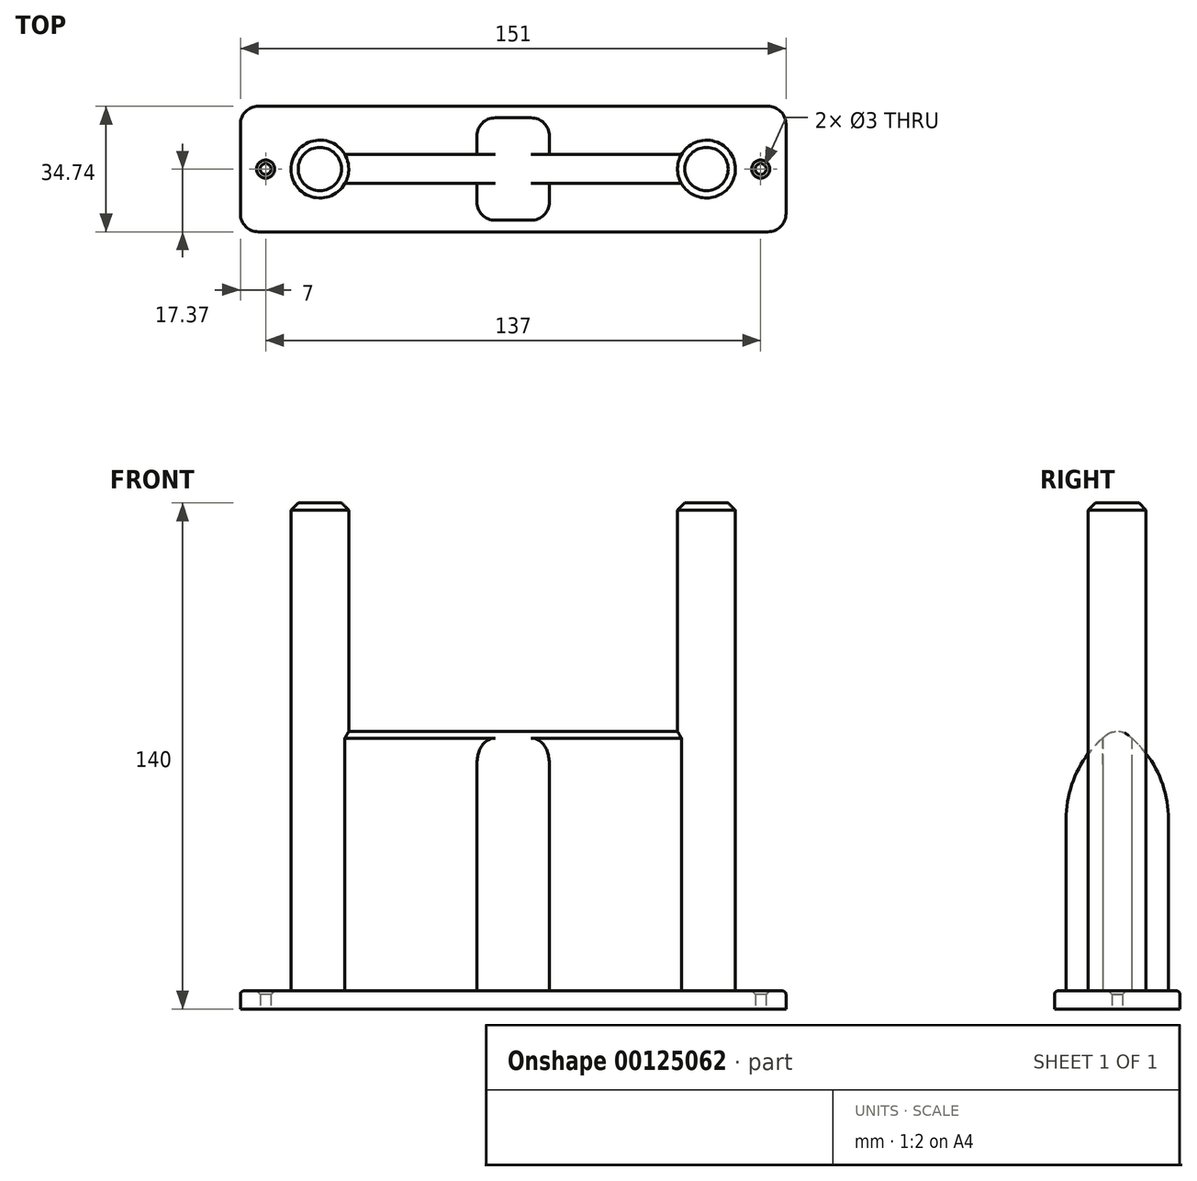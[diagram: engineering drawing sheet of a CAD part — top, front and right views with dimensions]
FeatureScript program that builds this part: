
annotation { "Feature Type Name" : "Feature", "Feature Type Description" : "" }
export const myFeature = defineFeature(function(context is Context, id is Id, definition is map)
    precondition{}
    {
        {
            var Q0;
            Q0=qCreatedBy(makeId("Top.planeOp"),FACE);
            var sketch = newSketch(context, id + "F0", { "sketchPlane" : qUnion([Q0])});
            skCircle(sketch, "E0", {"center": v(-53.5, 0) * mm, "radius": 8 * mm});
            skCircle(sketch, "E1", {"center": v(53.5, 0) * mm, "radius": 8 * mm});
            skLineSegment(sketch, "E2.bottom", {"start": v(-70.5, 17.37) * mm, "end": v(70.5, 17.37) * mm});
            skLineSegment(sketch, "E2.top", {"start": v(-70.5, -17.37) * mm, "end": v(70.5, -17.37) * mm});
            skLineSegment(sketch, "E2.left", {"start": v(-75.5, 12.37) * mm, "end": v(-75.5, -12.37) * mm});
            skLineSegment(sketch, "E2.right", {"start": v(75.5, 12.37) * mm, "end": v(75.5, -12.37) * mm});
            skPoint(sketch, "E2.middle", {"position": v(0, 0) * mm});
            skPoint(sketch, "E3.visualSharp", {"position": v(-75.5, 17.37) * mm});
            skArc(sketch, "E3.filletArc", {"start": v(-70.5, 17.37) * mm, "mid": v(-74.04, 15.9) * mm, "end": v(-75.5, 12.37) * mm});
            skPoint(sketch, "E4.visualSharp", {"position": v(75.5, 17.37) * mm});
            skArc(sketch, "E4.filletArc", {"start": v(75.5, 12.37) * mm, "mid": v(74.04, 15.9) * mm, "end": v(70.5, 17.37) * mm});
            skPoint(sketch, "E5.visualSharp", {"position": v(75.5, -17.37) * mm});
            skArc(sketch, "E5.filletArc", {"start": v(70.5, -17.37) * mm, "mid": v(74.04, -15.9) * mm, "end": v(75.5, -12.37) * mm});
            skPoint(sketch, "E6.visualSharp", {"position": v(-75.5, -17.37) * mm});
            skArc(sketch, "E6.filletArc", {"start": v(-75.5, -12.37) * mm, "mid": v(-74.04, -15.9) * mm, "end": v(-70.5, -17.37) * mm});
            skCircle(sketch, "E7", {"center": v(-68.5, 0) * mm, "radius": 1.5 * mm});
            skCircle(sketch, "E8", {"center": v(68.5, 0) * mm, "radius": 1.5 * mm});
            skLineSegment(sketch, "E9.bottom", {"start": v(-53.5, 4) * mm, "end": v(53.5, 4) * mm});
            skLineSegment(sketch, "E9.top", {"start": v(-53.5, -4) * mm, "end": v(53.5, -4) * mm});
            skLineSegment(sketch, "E9.left", {"start": v(-53.5, 4) * mm, "end": v(-53.5, -4) * mm});
            skLineSegment(sketch, "E9.right", {"start": v(53.5, 4) * mm, "end": v(53.5, -4) * mm});
            skLineSegment(sketch, "E10.bottom", {"start": v(10.01, 14.16) * mm, "end": v(-10.01, 14.16) * mm});
            skLineSegment(sketch, "E10.top", {"start": v(10.01, -14.16) * mm, "end": v(-10.01, -14.16) * mm});
            skLineSegment(sketch, "E10.left", {"start": v(10.01, 14.16) * mm, "end": v(10.01, -14.16) * mm});
            skLineSegment(sketch, "E10.right", {"start": v(-10.01, 14.16) * mm, "end": v(-10.01, -14.16) * mm});
            skSolve(sketch);
        }
        {
            var Q0;
            Q0=makeQuery(id+"F0.imprint","IMPRINT",FACE,{"disambiguationData":[TD([[makeQuery(id+"F0.imprint","IMPRINT",EDGE,{"derivedFrom":sQuery(id+"F0.wireOp",EDGE,"E0")}),-1.0]])]});
            var Q1;
            Q1=makeQuery(id+"F0.imprint","IMPRINT",FACE,{"disambiguationData":[TD([[makeQuery(id+"F0.imprint","IMPRINT",EDGE,{"derivedFrom":sQuery(id+"F0.wireOp",EDGE,"E2.bottom")}),-1.0]])]});
            var Q2;
            {var subQ5=sQuery(id+"F0.wireOp",EDGE,"E10.bottom");Q2=makeQuery(id+"F0.imprint","IMPRINT",FACE,{"disambiguationData":[TD([[makeQuery(id+"F0.imprint","IMPRINT",EDGE,{"derivedFrom":subQ5}),1.0]])]});}
            var Q3;
            {var subQ0=sQuery(id+"F0.wireOp",EDGE,"E10.right");var subQ1=sQuery(id+"F0.wireOp",EDGE,"E9.bottom");var subQ2=makeQuery(id+"F0.imprint","INTERSECT",VERTEX,{"derivedFrom":[subQ1,subQ0]});Q3=makeQuery(id+"F0.imprint","IMPRINT",FACE,{"disambiguationData":[TD([[makeQuery(id+"F0.imprint","IMPRINT",EDGE,{"disambiguationData":[TD([[subQ2,-1.0]])],"derivedFrom":subQ1}),-1.0]])]});}
            var Q4;
            {var subQ0=sQuery(id+"F0.wireOp",EDGE,"E9.bottom");var subQ1=sQuery(id+"F0.wireOp",EDGE,"E1");var subQ2=makeQuery(id+"F0.imprint","INTERSECT",VERTEX,{"derivedFrom":[subQ1,subQ0]});Q4=makeQuery(id+"F0.imprint","IMPRINT",FACE,{"disambiguationData":[TD([[makeQuery(id+"F0.imprint","IMPRINT",EDGE,{"disambiguationData":[TD([[subQ2,-1.0]])],"derivedFrom":subQ1}),-1.0]])]});}
            var Q5;
            {var subQ5=sQuery(id+"F0.wireOp",EDGE,"E10.top");Q5=makeQuery(id+"F0.imprint","IMPRINT",FACE,{"disambiguationData":[TD([[makeQuery(id+"F0.imprint","IMPRINT",EDGE,{"derivedFrom":subQ5}),-1.0]])]});}
            extrude(context, id + "F1", {"entities" : qUnion([Q0, Q1, Q2, Q3, Q4, Q5]), "depth" : 5 * mm});
        }
        {
            var Q0;
            Q0=makeQuery(id+"F0.imprint","IMPRINT",FACE,{"disambiguationData":[TD([[makeQuery(id+"F0.imprint","IMPRINT",EDGE,{"derivedFrom":sQuery(id+"F0.wireOp",EDGE,"E0")}),1.0]])]});
            var Q1;
            Q1=makeQuery(id+"F0.imprint","IMPRINT",FACE,{"disambiguationData":[TD([[makeQuery(id+"F0.imprint","IMPRINT",EDGE,{"derivedFrom":sQuery(id+"F0.wireOp",EDGE,"E1")}),1.0]])]});
            extrude(context, id + "F2", {"entities" : qUnion([Q0, Q1]), "operationType" : NewBodyOperationType.ADD, "depth" : 140 * mm});
        }
        {
            var Q0;
            Q0=makeQuery(id+"F2.opExtrude","CAP_EDGE",EDGE,{"disambiguationData":[OSD([sQuery(id+"F0.wireOp",EDGE,"E0")])],"isStart":false});
            var Q1;
            Q1=makeQuery(id+"F2.opExtrude","CAP_EDGE",EDGE,{"disambiguationData":[OSD([sQuery(id+"F0.wireOp",EDGE,"E1")])],"isStart":false});
            chamfer(context, id + "F3", {"entities" : qUnion([Q0, Q1]), "width" : 2 * mm, "tangentPropagation" : true});
        }
        {
            var Q0;
            Q0=makeQuery(id+"F1.opExtrude","CAP_EDGE",EDGE,{"disambiguationData":[OSD([sQuery(id+"F0.wireOp",EDGE,"E7")])],"isStart":false});
            var Q1;
            Q1=makeQuery(id+"F1.opExtrude","CAP_EDGE",EDGE,{"disambiguationData":[OSD([sQuery(id+"F0.wireOp",EDGE,"E8")])],"isStart":false});
            chamfer(context, id + "F4", {"entities" : qUnion([Q0, Q1]), "width" : 1 * mm, "tangentPropagation" : true});
        }
        {
            var Q0;
            Q0=makeQuery(id+"F1.opExtrude","CAP_EDGE",EDGE,{"disambiguationData":[OSD([sQuery(id+"F0.wireOp",EDGE,"E2.top")])],"isStart":false});
            fillet(context, id + "F5", {"entities" : qUnion([Q0]), "radius" : 1 * mm, "tangentPropagation" : true, "allowEdgeOverflow" : false});
        }
        {
            var Q0;
            {var subQ0=sQuery(id+"F0.wireOp",EDGE,"E9.bottom");var subQ1=sQuery(id+"F0.wireOp",EDGE,"E0");var subQ2=makeQuery(id+"F0.imprint","INTERSECT",VERTEX,{"derivedFrom":[subQ1,subQ0]});Q0=makeQuery(id+"F0.imprint","IMPRINT",FACE,{"disambiguationData":[TD([[makeQuery(id+"F0.imprint","IMPRINT",EDGE,{"disambiguationData":[TD([[subQ2,1.0]])],"derivedFrom":subQ1}),-1.0]])]});}
            var Q1;
            {var subQ0=sQuery(id+"F0.wireOp",EDGE,"E10.right");var subQ1=sQuery(id+"F0.wireOp",EDGE,"E9.bottom");var subQ2=makeQuery(id+"F0.imprint","INTERSECT",VERTEX,{"derivedFrom":[subQ1,subQ0]});Q1=makeQuery(id+"F0.imprint","IMPRINT",FACE,{"disambiguationData":[TD([[makeQuery(id+"F0.imprint","IMPRINT",EDGE,{"disambiguationData":[TD([[subQ2,-1.0]])],"derivedFrom":subQ1}),-1.0]])]});}
            var Q2;
            {var subQ0=sQuery(id+"F0.wireOp",EDGE,"E9.bottom");var subQ1=sQuery(id+"F0.wireOp",EDGE,"E1");var subQ2=makeQuery(id+"F0.imprint","INTERSECT",VERTEX,{"derivedFrom":[subQ1,subQ0]});Q2=makeQuery(id+"F0.imprint","IMPRINT",FACE,{"disambiguationData":[TD([[makeQuery(id+"F0.imprint","IMPRINT",EDGE,{"disambiguationData":[TD([[subQ2,-1.0]])],"derivedFrom":subQ1}),-1.0]])]});}
            var Q3;
            {var subQ5=sQuery(id+"F0.wireOp",EDGE,"E10.bottom");Q3=makeQuery(id+"F0.imprint","IMPRINT",FACE,{"disambiguationData":[TD([[makeQuery(id+"F0.imprint","IMPRINT",EDGE,{"derivedFrom":subQ5}),1.0]])]});}
            var Q4;
            {var subQ5=sQuery(id+"F0.wireOp",EDGE,"E10.top");Q4=makeQuery(id+"F0.imprint","IMPRINT",FACE,{"disambiguationData":[TD([[makeQuery(id+"F0.imprint","IMPRINT",EDGE,{"derivedFrom":subQ5}),-1.0]])]});}
            extrude(context, id + "F6", {"entities" : qUnion([Q0, Q1, Q2, Q3, Q4]), "operationType" : NewBodyOperationType.ADD, "depth" : 80 * mm});
        }
        {
            var Q0;
            Q0=makeQuery(id+"F6.opExtrude","CAP_EDGE",EDGE,{"disambiguationData":[OSD([sQuery(id+"F0.wireOp",EDGE,"E10.top")])],"isStart":false});
            var Q1;
            Q1=makeQuery(id+"F6.opExtrude","CAP_EDGE",EDGE,{"disambiguationData":[OSD([sQuery(id+"F0.wireOp",EDGE,"E10.bottom")])],"isStart":false});
            fillet(context, id + "F7", {"entities" : qUnion([Q0, Q1]), "radius" : 30 * mm, "allowEdgeOverflow" : false});
        }
        {
            var Q0;
            Q0=makeQuery(id+"F7.opFillet","BLEND_EDGE",EDGE,{"blendedFrom":[makeQuery(id+"F6.opExtrude","CAP_EDGE",EDGE,{"disambiguationData":[OSD([sQuery(id+"F0.wireOp",EDGE,"E10.bottom")])],"isStart":false}),makeQuery(id+"F6.opExtrude","CAP_EDGE",EDGE,{"disambiguationData":[OSD([sQuery(id+"F0.wireOp",EDGE,"E10.top")])],"isStart":false})],"blendedInto":[]});
            fillet(context, id + "F8", {"entities" : qUnion([Q0]), "radius" : 5 * mm, "tangentPropagation" : true, "allowEdgeOverflow" : false});
        }
        {
            var Q0;
            {var subQ0=sQuery(id+"F0.wireOp",EDGE,"E10.left");var subQ1=sQuery(id+"F0.wireOp",EDGE,"E10.bottom");Q0=makeQuery(id+"F7.opFillet","BLEND_EDGE",EDGE,{"blendedFrom":[makeQuery(id+"F6.opExtrude","CAP_EDGE",EDGE,{"disambiguationData":[OSD([subQ1])],"isStart":false}),makeQuery(id+"F6.opExtrude","SWEPT_FACE",FACE,{"disambiguationData":[OSD([subQ0]),TDD([makeQuery(id+"F0.imprint","IMPRINT",EDGE,{"disambiguationData":[TD([[makeQuery(id+"F0.imprint","INTERSECT",VERTEX,{"derivedFrom":[subQ1,subQ0]}),-1.0]])],"derivedFrom":subQ0})])]})],"blendedInto":[makeQuery(id+"F6.opExtrude","SWEPT_FACE",FACE,{"disambiguationData":[OSD([subQ0]),TDD([makeQuery(id+"F0.imprint","IMPRINT",EDGE,{"disambiguationData":[TD([[makeQuery(id+"F0.imprint","INTERSECT",VERTEX,{"derivedFrom":[subQ1,subQ0]}),-1.0]])],"derivedFrom":subQ0})])]})]});}
            var Q1;
            {var subQ0=sQuery(id+"F0.wireOp",EDGE,"E10.right");var subQ1=sQuery(id+"F0.wireOp",EDGE,"E10.bottom");Q1=makeQuery(id+"F7.opFillet","BLEND_EDGE",EDGE,{"blendedFrom":[makeQuery(id+"F6.opExtrude","CAP_EDGE",EDGE,{"disambiguationData":[OSD([subQ1])],"isStart":false}),makeQuery(id+"F6.opExtrude","SWEPT_FACE",FACE,{"disambiguationData":[OSD([subQ0]),TDD([makeQuery(id+"F0.imprint","IMPRINT",EDGE,{"disambiguationData":[TD([[makeQuery(id+"F0.imprint","INTERSECT",VERTEX,{"derivedFrom":[subQ1,subQ0]}),-1.0]])],"derivedFrom":subQ0})])]})],"blendedInto":[makeQuery(id+"F6.opExtrude","SWEPT_FACE",FACE,{"disambiguationData":[OSD([subQ0]),TDD([makeQuery(id+"F0.imprint","IMPRINT",EDGE,{"disambiguationData":[TD([[makeQuery(id+"F0.imprint","INTERSECT",VERTEX,{"derivedFrom":[subQ1,subQ0]}),-1.0]])],"derivedFrom":subQ0})])]})]});}
            var Q2;
            {var subQ0=sQuery(id+"F0.wireOp",EDGE,"E10.left");var subQ1=sQuery(id+"F0.wireOp",EDGE,"E10.top");Q2=makeQuery(id+"F7.opFillet","BLEND_EDGE",EDGE,{"blendedFrom":[makeQuery(id+"F6.opExtrude","CAP_EDGE",EDGE,{"disambiguationData":[OSD([subQ1])],"isStart":false}),makeQuery(id+"F6.opExtrude","SWEPT_FACE",FACE,{"disambiguationData":[OSD([subQ0]),TDD([makeQuery(id+"F0.imprint","IMPRINT",EDGE,{"disambiguationData":[TD([[makeQuery(id+"F0.imprint","INTERSECT",VERTEX,{"derivedFrom":[subQ1,subQ0]}),1.0]])],"derivedFrom":subQ0})])]})],"blendedInto":[makeQuery(id+"F6.opExtrude","SWEPT_FACE",FACE,{"disambiguationData":[OSD([subQ0]),TDD([makeQuery(id+"F0.imprint","IMPRINT",EDGE,{"disambiguationData":[TD([[makeQuery(id+"F0.imprint","INTERSECT",VERTEX,{"derivedFrom":[subQ1,subQ0]}),1.0]])],"derivedFrom":subQ0})])]})]});}
            var Q3;
            {var subQ0=sQuery(id+"F0.wireOp",EDGE,"E10.right");var subQ1=sQuery(id+"F0.wireOp",EDGE,"E10.top");Q3=makeQuery(id+"F7.opFillet","BLEND_EDGE",EDGE,{"blendedFrom":[makeQuery(id+"F6.opExtrude","CAP_EDGE",EDGE,{"disambiguationData":[OSD([subQ1])],"isStart":false}),makeQuery(id+"F6.opExtrude","SWEPT_FACE",FACE,{"disambiguationData":[OSD([subQ0]),TDD([makeQuery(id+"F0.imprint","IMPRINT",EDGE,{"disambiguationData":[TD([[makeQuery(id+"F0.imprint","INTERSECT",VERTEX,{"derivedFrom":[subQ1,subQ0]}),1.0]])],"derivedFrom":subQ0})])]})],"blendedInto":[makeQuery(id+"F6.opExtrude","SWEPT_FACE",FACE,{"disambiguationData":[OSD([subQ0]),TDD([makeQuery(id+"F0.imprint","IMPRINT",EDGE,{"disambiguationData":[TD([[makeQuery(id+"F0.imprint","INTERSECT",VERTEX,{"derivedFrom":[subQ1,subQ0]}),1.0]])],"derivedFrom":subQ0})])]})]});}
            fillet(context, id + "F9", {"entities" : qUnion([Q0, Q1, Q2, Q3]), "radius" : 5 * mm, "tangentPropagation" : true, "allowEdgeOverflow" : false});
        }
    });
